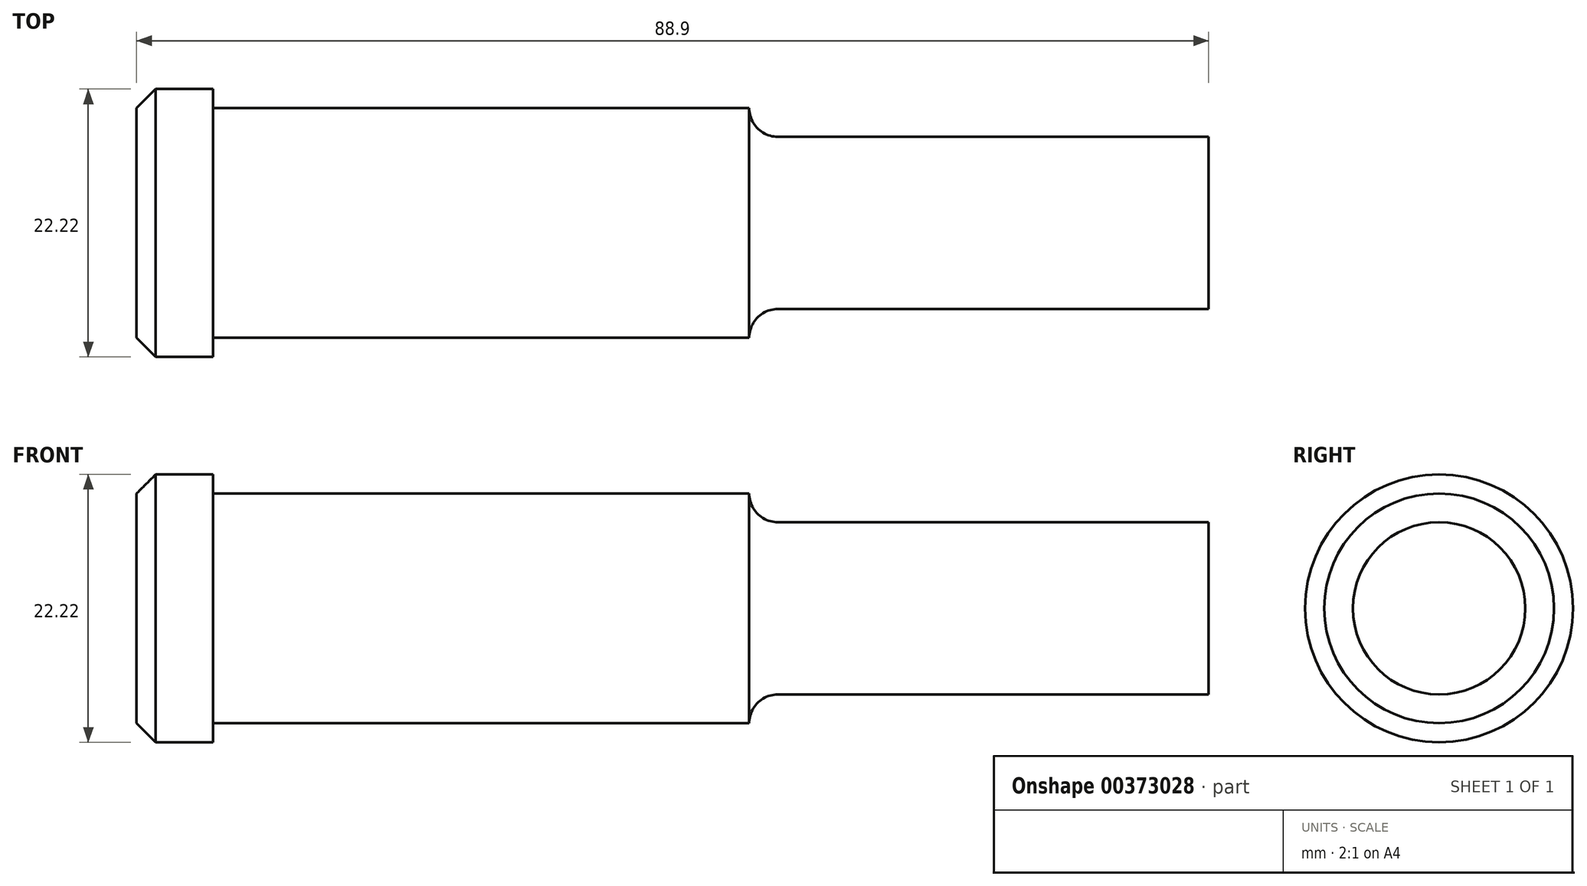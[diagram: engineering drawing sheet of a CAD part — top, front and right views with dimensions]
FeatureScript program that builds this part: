
annotation { "Feature Type Name" : "Feature", "Feature Type Description" : "" }
export const myFeature = defineFeature(function(context is Context, id is Id, definition is map)
    precondition{}
    {
        {
            var Q0;
            Q0=qCreatedBy(makeId("Front.planeOp"),FACE);
            var sketch = newSketch(context, id + "F0", { "sketchPlane" : qUnion([Q0])});
            skLineSegment(sketch, "E0", {"start": v(-29.43, 0) * mm, "end": v(-29.43, 11.11) * mm});
            skLineSegment(sketch, "E1", {"start": v(-29.43, 11.11) * mm, "end": v(-23.08, 11.11) * mm});
            skLineSegment(sketch, "E2", {"start": v(-23.08, 11.11) * mm, "end": v(-23.08, 9.52) * mm});
            skLineSegment(sketch, "E3", {"start": v(-23.08, 9.52) * mm, "end": v(21.37, 9.53) * mm});
            skLineSegment(sketch, "E4", {"start": v(59.47, 7.14) * mm, "end": v(59.47, 0) * mm});
            skPoint(sketch, "E5.second.point", {"position": v(23.07, 17.53) * mm});
            skPoint(sketch, "E5.third.point", {"position": v(34.35, 13) * mm});
            skLineSegment(sketch, "E6", {"start": v(-29.43, 0) * mm, "end": v(59.47, 0) * mm});
            skLineSegment(sketch, "E7", {"start": v(59.47, 7.14) * mm, "end": v(23.75, 7.14) * mm});
            skArc(sketch, "E8", {"start": v(21.37, 9.53) * mm, "mid": v(22.06, 7.84) * mm, "end": v(23.75, 7.14) * mm});
            skSolve(sketch);
        }
        {
            var Q0;
            Q0=makeQuery(id+"F0.imprint","IMPRINT",FACE,{"disambiguationData":[TD([[makeQuery(id+"F0.imprint","IMPRINT",EDGE,{"derivedFrom":sQuery(id+"F0.wireOp",EDGE,"E0")}),-1.0]])]});
            var Q1;
            Q1=sQuery(id+"F0.wireOp",EDGE,"E6");
            revolve(context, id + "F1", {"surfaceOperationType" : NewSurfaceOperationType.NEW, "entities" : qUnion([Q0]), "axis" : qUnion([Q1]), "revolveType" : RevolveType.FULL});
        }
        {
            var Q0;
            Q0=makeQuery(id+"F1.opRevolve","SWEPT_EDGE",EDGE,{"disambiguationData":[OSD([sQuery(id+"F0.wireOp",EDGE,"E0"),sQuery(id+"F0.wireOp",EDGE,"E1")])]});
            chamfer(context, id + "F2", {"entities" : qUnion([Q0]), "width" : 1.59 * mm, "tangentPropagation" : true});
        }
    });
